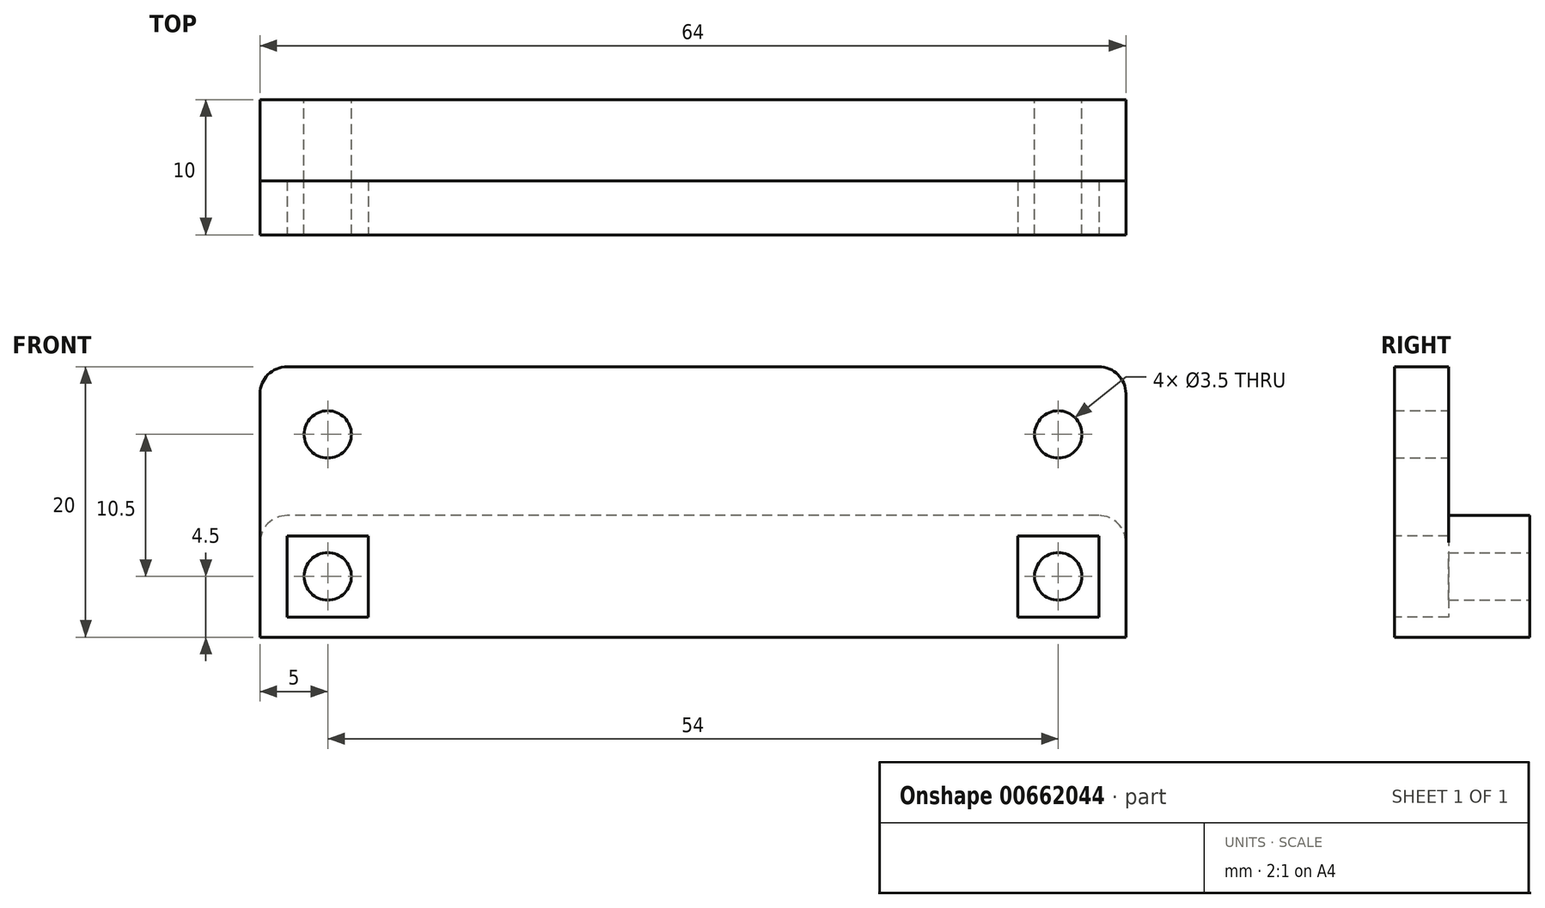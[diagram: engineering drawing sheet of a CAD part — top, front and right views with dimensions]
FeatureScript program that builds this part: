
annotation { "Feature Type Name" : "Feature", "Feature Type Description" : "" }
export const myFeature = defineFeature(function(context is Context, id is Id, definition is map)
    precondition{}
    {
        {
            var Q0;
            Q0=qCreatedBy(makeId("Front.planeOp"),FACE);
            var sketch = newSketch(context, id + "F0", { "sketchPlane" : qUnion([Q0])});
            skLineSegment(sketch, "E0.bottom", {"start": v(-32, 5) * mm, "end": v(32, 5) * mm});
            skLineSegment(sketch, "E0.top", {"start": v(-32, -5) * mm, "end": v(32, -5) * mm});
            skLineSegment(sketch, "E0.left", {"start": v(-32, 5) * mm, "end": v(-32, -5) * mm});
            skLineSegment(sketch, "E0.right", {"start": v(32, 5) * mm, "end": v(32, -5) * mm});
            skPoint(sketch, "E0.middle", {"position": v(0, 0) * mm});
            skLineSegment(sketch, "E1", {"start": v(0, 0) * mm, "end": v(-27, 0) * mm});
            skLineSegment(sketch, "E2", {"start": v(0, 0) * mm, "end": v(27, 0) * mm});
            skCircle(sketch, "E3", {"center": v(-27, 0) * mm, "radius": 1.75 * mm});
            skCircle(sketch, "E4", {"center": v(27, 0) * mm, "radius": 1.75 * mm});
            skSolve(sketch);
        }
        {
            var Q0;
            Q0=makeQuery(id+"F0.imprint","IMPRINT",FACE,{"disambiguationData":[TD([[makeQuery(id+"F0.imprint","IMPRINT",EDGE,{"derivedFrom":sQuery(id+"F0.wireOp",EDGE,"E0.bottom")}),-1.0]])]});
            extrude(context, id + "F1", {"entities" : qUnion([Q0]), "depth" : 4 * mm, "offsetDistance" : 25 * mm});
        }
        {
            var Q0;
            Q0=makeQuery(id+"F1.opExtrude","SWEPT_EDGE",EDGE,{"disambiguationData":[OSD([sQuery(id+"F0.wireOp",EDGE,"E0.bottom"),sQuery(id+"F0.wireOp",EDGE,"E0.left")])]});
            var Q1;
            Q1=makeQuery(id+"F1.opExtrude","SWEPT_EDGE",EDGE,{"disambiguationData":[OSD([sQuery(id+"F0.wireOp",EDGE,"E0.bottom"),sQuery(id+"F0.wireOp",EDGE,"E0.right")])]});
            fillet(context, id + "F2", {"entities" : qUnion([Q0, Q1]), "radius" : 2 * mm, "tangentPropagation" : true, "allowEdgeOverflow" : false});
        }
        {
            var Q0;
            Q0=makeQuery(id+"F1.opExtrude","SWEPT_FACE",FACE,{"disambiguationData":[OSD([sQuery(id+"F0.wireOp",EDGE,"E0.top")])]});
            extrude(context, id + "F3", {"entities" : qUnion([Q0]), "operationType" : NewBodyOperationType.ADD, "depth" : 10 * mm, "offsetDistance" : 25 * mm});
        }
        {
            var Q0;
            {var subQ0=sQuery(id+"F0.wireOp",EDGE,"E0.top");Q0=makeQuery(id+"F3.boolean.opBoolean","MERGE",FACE,{"derivedFrom":[makeQuery(id+"F1.opExtrude","CAP_FACE",FACE,{"disambiguationData":[OSD([sQuery(id+"F0.wireOp",EDGE,"E0.bottom"),subQ0,sQuery(id+"F0.wireOp",EDGE,"E0.left"),sQuery(id+"F0.wireOp",EDGE,"E0.right"),sQuery(id+"F0.wireOp",EDGE,"E3"),sQuery(id+"F0.wireOp",EDGE,"E4")])],"isStart":true}),makeQuery(id+"F3.opExtrude","SWEPT_FACE",FACE,{"disambiguationData":[OSD([subQ0]),TDD([makeQuery(id+"F1.opExtrude","CAP_EDGE",EDGE,{"disambiguationData":[OSD([subQ0])],"isStart":true})])]})]});}
            var sketch = newSketch(context, id + "F4", { "sketchPlane" : qUnion([Q0])});
            skLineSegment(sketch, "E5.bottom", {"start": v(-32, -6) * mm, "end": v(32, -6) * mm});
            skLineSegment(sketch, "E5.top", {"start": v(-32, -15) * mm, "end": v(32, -15) * mm});
            skLineSegment(sketch, "E5.left", {"start": v(-32, -6) * mm, "end": v(-32, -15) * mm});
            skLineSegment(sketch, "E5.right", {"start": v(32, -6) * mm, "end": v(32, -15) * mm});
            skSolve(sketch);
        }
        {
            var Q0;
            Q0 = qSketchRegion(id + "F4", true);
            extrude(context, id + "F5", {"entities" : qUnion([Q0]), "operationType" : NewBodyOperationType.ADD, "depth" : 6 * mm, "offsetDistance" : 25 * mm});
        }
        {
            var Q0;
            Q0=makeQuery(id+"F5.opExtrude","CAP_FACE",FACE,{"disambiguationData":[OSD([sQuery(id+"F4.wireOp",EDGE,"E5.bottom"),sQuery(id+"F4.wireOp",EDGE,"E5.top"),sQuery(id+"F4.wireOp",EDGE,"E5.left"),sQuery(id+"F4.wireOp",EDGE,"E5.right")])],"isStart":false});
            var sketch = newSketch(context, id + "F6", { "sketchPlane" : qUnion([Q0])});
            skLineSegment(sketch, "E6", {"start": v(-32, -10.5) * mm, "end": v(-27, -10.5) * mm});
            skLineSegment(sketch, "E7", {"start": v(32, -10.5) * mm, "end": v(27, -10.5) * mm});
            skCircle(sketch, "E8", {"center": v(-27, -10.5) * mm, "radius": 1.75 * mm});
            skCircle(sketch, "E9", {"center": v(27, -10.5) * mm, "radius": 1.75 * mm});
            skSolve(sketch);
        }
        {
            var Q0;
            Q0 = qSketchRegion(id + "F6", true);
            extrude(context, id + "F7", {"entities" : qUnion([Q0]), "operationType" : NewBodyOperationType.REMOVE, "oppositeDirection" : true, "depth" : 25 * mm, "offsetDistance" : 25 * mm});
        }
        {
            var Q0;
            {var subQ0=sQuery(id+"F0.wireOp",EDGE,"E0.top");Q0=makeQuery(id+"F3.boolean.opBoolean","MERGE",FACE,{"derivedFrom":[makeQuery(id+"F1.opExtrude","CAP_FACE",FACE,{"disambiguationData":[OSD([sQuery(id+"F0.wireOp",EDGE,"E0.bottom"),subQ0,sQuery(id+"F0.wireOp",EDGE,"E0.left"),sQuery(id+"F0.wireOp",EDGE,"E0.right"),sQuery(id+"F0.wireOp",EDGE,"E3"),sQuery(id+"F0.wireOp",EDGE,"E4")])],"isStart":false}),makeQuery(id+"F3.opExtrude","SWEPT_FACE",FACE,{"disambiguationData":[OSD([subQ0]),TDD([makeQuery(id+"F1.opExtrude","CAP_EDGE",EDGE,{"disambiguationData":[OSD([subQ0])],"isStart":false})])]})]});}
            var sketch = newSketch(context, id + "F8", { "sketchPlane" : qUnion([Q0])});
            skLineSegment(sketch, "E10.bottom", {"start": v(-30, -7.5) * mm, "end": v(-24, -7.5) * mm});
            skLineSegment(sketch, "E10.top", {"start": v(-30, -13.5) * mm, "end": v(-24, -13.5) * mm});
            skLineSegment(sketch, "E10.left", {"start": v(-30, -7.5) * mm, "end": v(-30, -13.5) * mm});
            skLineSegment(sketch, "E10.right", {"start": v(-24, -7.5) * mm, "end": v(-24, -13.5) * mm});
            skPoint(sketch, "E10.middle", {"position": v(-27, -10.5) * mm});
            skLineSegment(sketch, "E11.bottom", {"start": v(24, -7.5) * mm, "end": v(30, -7.5) * mm});
            skLineSegment(sketch, "E11.top", {"start": v(24, -13.5) * mm, "end": v(30, -13.5) * mm});
            skLineSegment(sketch, "E11.left", {"start": v(24, -7.5) * mm, "end": v(24, -13.5) * mm});
            skLineSegment(sketch, "E11.right", {"start": v(30, -7.5) * mm, "end": v(30, -13.5) * mm});
            skPoint(sketch, "E11.middle", {"position": v(27, -10.5) * mm});
            skSolve(sketch);
        }
        {
            var Q0;
            Q0 = qSketchRegion(id + "F8", true);
            extrude(context, id + "F9", {"entities" : qUnion([Q0]), "operationType" : NewBodyOperationType.REMOVE, "oppositeDirection" : true, "depth" : 4 * mm, "offsetDistance" : 25 * mm});
        }
        {
            var Q0;
            Q0=makeQuery(id+"F5.opExtrude","SWEPT_EDGE",EDGE,{"disambiguationData":[OSD([sQuery(id+"F0.wireOp",EDGE,"E0.top"),sQuery(id+"F0.wireOp",EDGE,"E0.right"),sQuery(id+"F4.wireOp",EDGE,"E5.bottom"),sQuery(id+"F4.wireOp",EDGE,"E5.left")])]});
            var Q1;
            Q1=makeQuery(id+"F5.opExtrude","SWEPT_EDGE",EDGE,{"disambiguationData":[OSD([sQuery(id+"F0.wireOp",EDGE,"E0.top"),sQuery(id+"F0.wireOp",EDGE,"E0.left"),sQuery(id+"F4.wireOp",EDGE,"E5.bottom"),sQuery(id+"F4.wireOp",EDGE,"E5.right")])]});
            fillet(context, id + "F10", {"entities" : qUnion([Q0, Q1]), "radius" : 2 * mm, "tangentPropagation" : true, "allowEdgeOverflow" : false});
        }
    });
